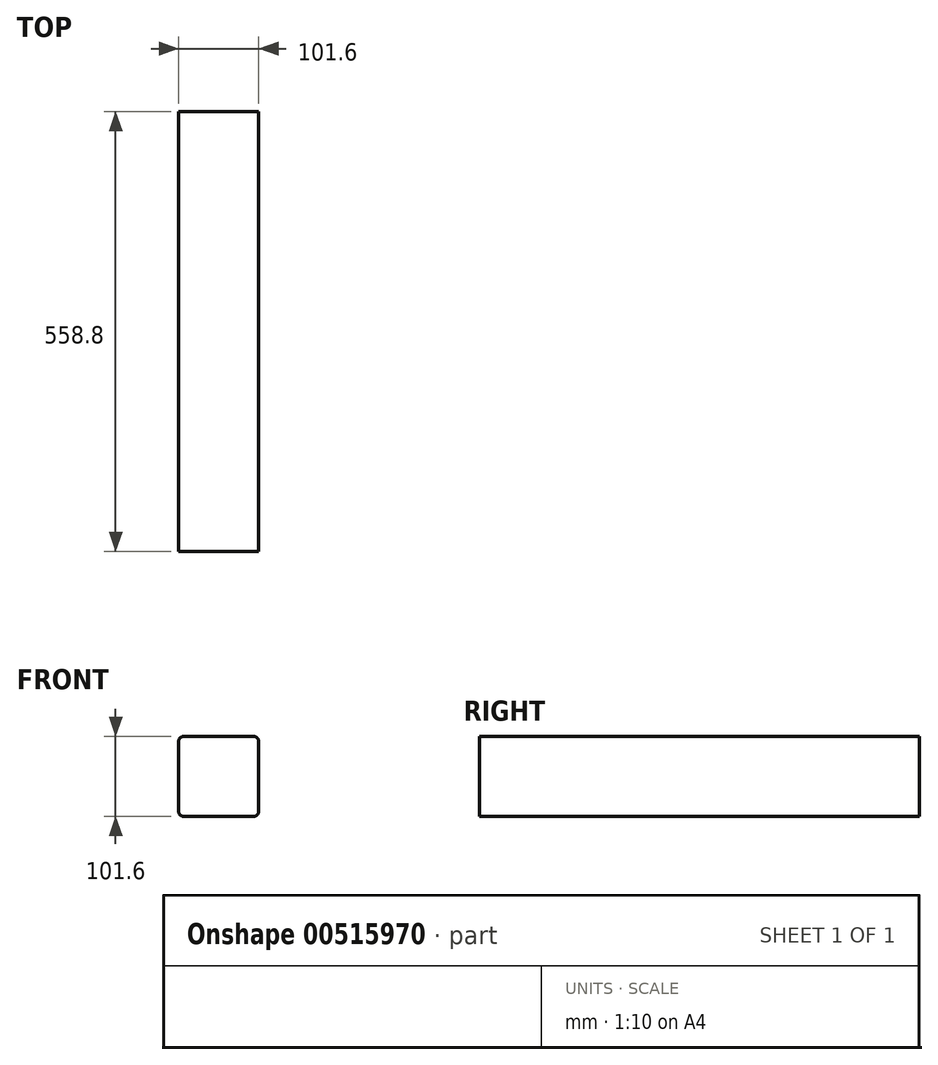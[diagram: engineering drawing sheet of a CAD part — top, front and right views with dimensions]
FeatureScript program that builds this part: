
annotation { "Feature Type Name" : "Feature", "Feature Type Description" : "" }
export const myFeature = defineFeature(function(context is Context, id is Id, definition is map)
    precondition{}
    {
        {
            var Q0;
            Q0=qCreatedBy(makeId("Front.planeOp"),FACE);
            var sketch = newSketch(context, id + "F0", { "sketchPlane" : qUnion([Q0])});
            skLineSegment(sketch, "E0.bottom", {"start": v(44.45, 52.86) * mm, "end": v(-44.45, 52.86) * mm});
            skLineSegment(sketch, "E0.top", {"start": v(44.45, -48.74) * mm, "end": v(-44.45, -48.74) * mm});
            skLineSegment(sketch, "E0.left", {"start": v(50.8, 46.51) * mm, "end": v(50.8, -42.39) * mm});
            skLineSegment(sketch, "E0.right", {"start": v(-50.8, 46.51) * mm, "end": v(-50.8, -42.39) * mm});
            skPoint(sketch, "E0.middle", {"position": v(0, 0) * mm});
            skArc(sketch, "E1", {"start": v(-44.45, 52.86) * mm, "mid": v(-48.94, 51) * mm, "end": v(-50.8, 46.51) * mm});
            skArc(sketch, "E2", {"start": v(50.8, 46.51) * mm, "mid": v(48.94, 51) * mm, "end": v(44.45, 52.86) * mm});
            skArc(sketch, "E3", {"start": v(-50.8, -42.39) * mm, "mid": v(-48.94, -46.88) * mm, "end": v(-44.45, -48.74) * mm});
            skArc(sketch, "E4", {"start": v(44.45, -48.74) * mm, "mid": v(48.94, -46.88) * mm, "end": v(50.8, -42.39) * mm});
            skSolve(sketch);
        }
        {
            var Q0;
            Q0=makeQuery(id+"F0.imprint","IMPRINT",FACE,{"disambiguationData":[TD([[makeQuery(id+"F0.imprint","IMPRINT",EDGE,{"derivedFrom":sQuery(id+"F0.wireOp",EDGE,"E0.bottom")}),1.0]])]});
            extrude(context, id + "F1", {"entities" : qUnion([Q0]), "depth" : 558.8 * mm, "offsetDistance" : 25.4 * mm});
        }
    });
